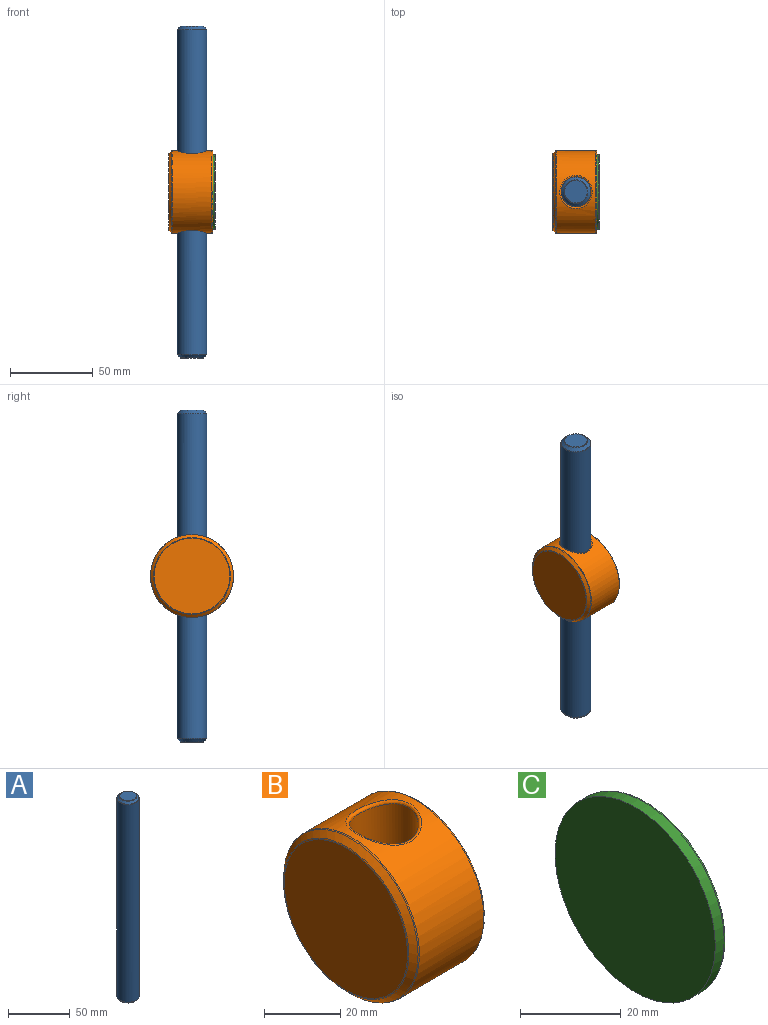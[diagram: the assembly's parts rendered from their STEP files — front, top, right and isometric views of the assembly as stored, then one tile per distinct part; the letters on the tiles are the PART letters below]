
ASSEMBLY  parts=3 mates=2
PART A: 9 faces, bbox 19.5x19.5x200 mm
  f0: cylinder r=9mm len=195.59mm, axis (0,0,-1), area 11060.1mm2, adj f6,f7
  f1: plane 13.59x13.59mm, normal (0,0,1), area 145mm2, adj f8
  f2: plane 13.59x13.59mm, normal (0,0,-1), area 145mm2, adj f5
  f3: cone r=7mm half-angle=45deg, axis (0,0,-1), area 121.4mm2, adj f6,f8
  f4: cone r=9mm half-angle=45deg, axis (0,0,1), area 121.4mm2, adj f5,f7
  f5: torus R=6.79mm, axis (0,0,1), area 17.2mm2, adj f2,f4
  f6: torus R=8.5mm, axis (0,0,1), area 22.1mm2, adj f0,f3
  f7: torus R=8.5mm, axis (0,0,-1), area 22.1mm2, adj f0,f4
  f8: torus R=6.79mm, axis (0,0,1), area 17.2mm2, adj f1,f3
PART B: 15 faces, bbox 26.5x54.1x54.1 mm
  f0: cylinder r=25mm len=50mm, axis (-1,0,0), area 3109.1mm2, adj f7,f8,f13,f14
  f1: plane 49x49mm, normal (1,0,0), area 193.8mm2, adj f11,f14
  f2: plane 45.59x45.59mm, normal (-1,0,0), area 1632.1mm2, adj f12
  f3: cylinder r=22.5mm len=45mm, axis (-1,0,0), area 112.1mm2, adj f4,f10
  f4: plane 45x45mm, normal (1,0,0), area 1590.4mm2, adj f3
  f5: cylinder r=9mm len=48.5mm, axis (0,0,-1), area 2628mm2, adj f7,f8
  f6: cone r=25mm half-angle=45deg, axis (1,0,0), area 364.1mm2, adj f12,f13
  f7: bspline ~20.13x19.5mm, area 78.9mm2, adj f0,f5
  f8: bspline ~20.13x19.5mm, area 78.9mm2, adj f0,f5
  f9: cone r=23mm half-angle=45deg, axis (1,0,0), area 41.9mm2, adj f10,f11
  f10: torus R=23mm, axis (-1,0,0), area 55.6mm2, adj f3,f9
  f11: torus R=23.21mm, axis (1,0,0), area 56.8mm2, adj f1,f9
  f12: torus R=22.79mm, axis (1,0,0), area 56.7mm2, adj f2,f6
  f13: torus R=24.5mm, axis (-1,0,0), area 61.6mm2, adj f0,f6
  f14: torus R=24.5mm, axis (1,0,0), area 122.5mm2, adj f0,f1
PART C: 4 faces, bbox 3x48.7x48.7 mm
  f0: cylinder r=22.5mm len=45mm, axis (-1,0,0), area 353.4mm2, adj f2,f3
  f1: plane 44x44mm, normal (1,0,0), area 1520.5mm2, adj f3
  f2: plane 45x45mm, normal (-1,0,0), area 1590.4mm2, adj f0
  f3: torus R=22mm, axis (1,0,0), area 110.1mm2, adj f0,f1
PLACE A t=(-14,0,0)mm
PLACE B t=(-14,0,0)mm
PLACE C t=(-14,0,0)mm
MATE fastened A.f0 <-> B.f5  axis (0,0,-1) through (-14,0,0)mm
MATE fastened C.f0 <-> B.f3  axis (-1,0,0) through (-3,0,0)mm
